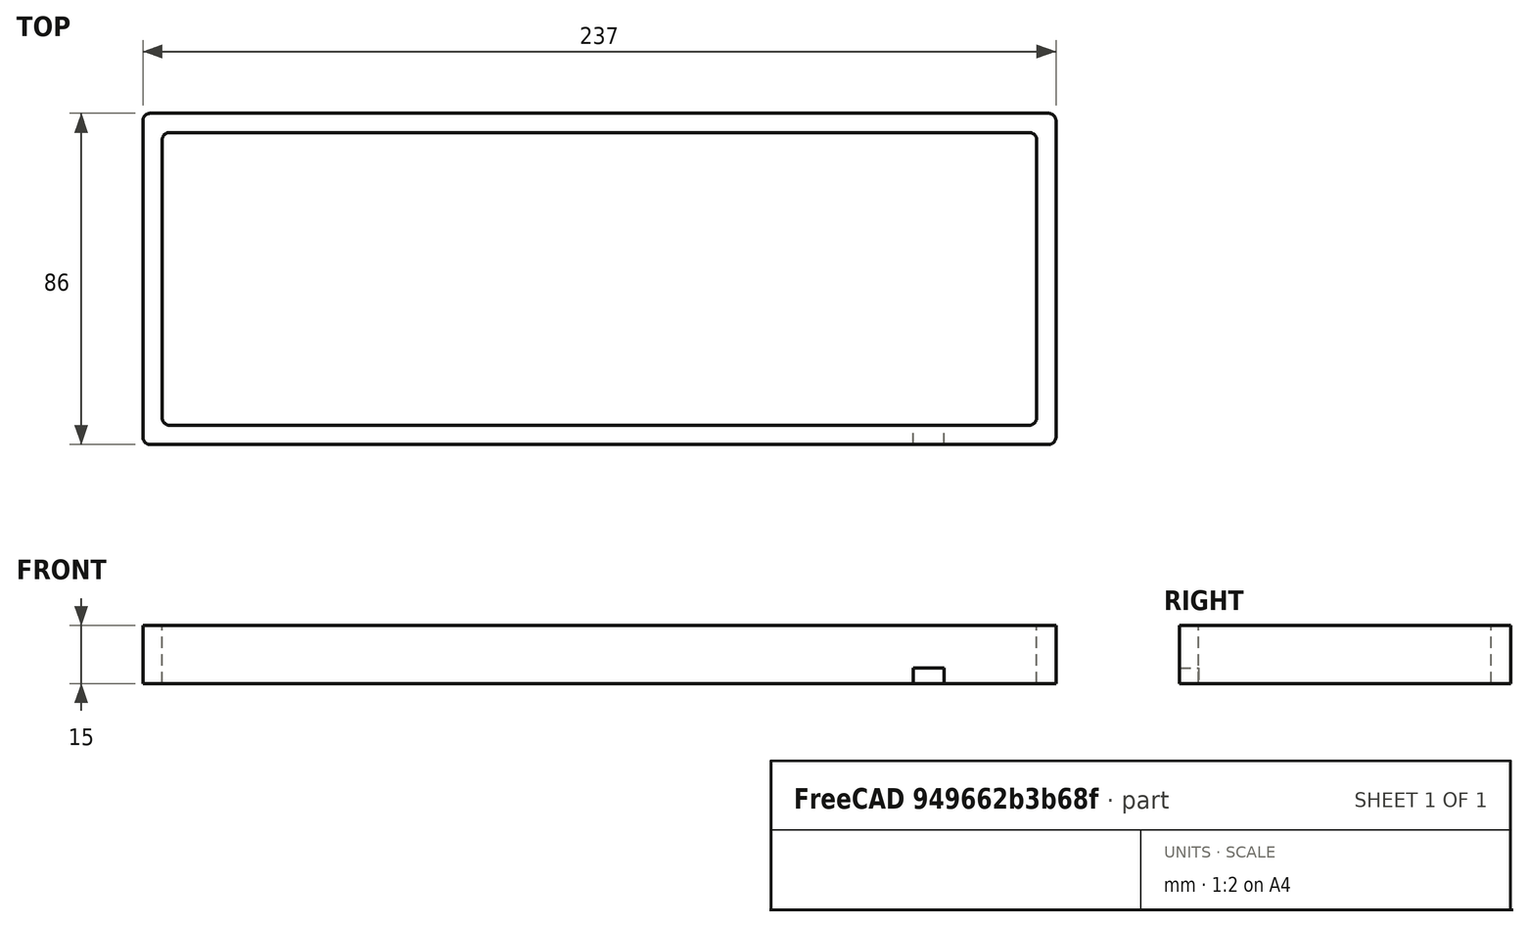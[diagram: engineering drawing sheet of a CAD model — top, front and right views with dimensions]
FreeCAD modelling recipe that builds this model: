
FCSTD DOCUMENT  (FreeCAD 0.16RUnknown)
Label: case
License: All rights reserved
LicenseURL: http://en.wikipedia.org/wiki/All_rights_reserved
objects: App::MeasureDistance×6, Part::Extrusion×3, Part::Part2DObjectPython×2, Part::Cut×2, Part::Box×1
note: 8 computed .brp shape members not serialized (recipe doc carries the construction recipe); baked Part::Feature solids carry a one-line shape summary decoded from their .brp

FEATURE [Part::Part2DObjectPython] Rectangle  # Draft 2D object (typed FeaturePython)
  ChamferSize = 0
  Columns = 1
  FilletRadius = 2
  Height = 76
  Length = 227
  MakeFace = true
  Placement = pos=(5,5,0) rot=(0,0,1;0rad)
  Rows = 1
FEATURE [Part::Part2DObjectPython] Rectangle001  # Draft 2D object (typed FeaturePython)
  ChamferSize = 0
  Columns = 1
  FilletRadius = 2
  Height = 86
  Length = 237
  MakeFace = true
  Rows = 1
FEATURE [Part::Extrusion] Extrude
  Base = -> Rectangle
  Dir = (0,0,15)
  Solid = true
FEATURE [Part::Extrusion] Extrude001
  Base = -> Rectangle001
  Dir = (0,0,15)
  Solid = true
FEATURE [Part::Extrusion] Extrude002
  Base = -> Rectangle001
  Dir = (0,0,15)
  Solid = true
FEATURE [Part::Cut] Cut
  Base = -> Extrude001
  Tool = -> Extrude
FEATURE [Part::Box] Box  label="Cube"
  Height = 4
  Length = 8
  Placement = pos=(200,0,0) rot=(0,0,1;0rad)
  Width = 8
FEATURE [Part::Cut] Cut001
  Base = -> Cut
  Tool = -> Box
FEATURE [App::MeasureDistance] Distance  label="Distance: 86 mm"
  Distance = 86
  P1 = (235,86,15)
  P2 = (234.998,0,15)
FEATURE [App::MeasureDistance] Distance001  label="Distance: 236.995 mm"
  Distance = 236.995
  P1 = (236.995,1.96437,15)
  P2 = (0,2,15)
FEATURE [App::MeasureDistance] Distance002  label="Distance: 5.00026 mm"
  Distance = 5.00026
  P1 = (0,39.7839,15)
  P2 = (5,39.7328,15)
FEATURE [App::MeasureDistance] Distance003  label="Distance: 8.01666 mm"
  Distance = 8.01666
  P1 = (199.997,0,0)
  P2 = (208.014,0,0.00131472)
FEATURE [App::MeasureDistance] Distance004  label="Distance: 3.97675 mm"
  Distance = 3.97675
  P1 = (200,0,3.97675)
  P2 = (200,0,0)
FEATURE [App::MeasureDistance] Distance005  label="Distance: 15 mm"
  Distance = 15
  P1 = (237,83.9635,15)
  P2 = (237,84,0)
